# Revit family: STS-750_RV17_LOD_400
name_source: partatom
category: Электрооборудование
revit_build: Autodesk Revit 2017 (Build: 20170118_1100(x64)
units: mm (PartAtom-declared; Revit-internal decimal feet)

## family parameters
Всегда вертикально = Да
Конфигурация панели = Два столбца, слева направо
На основе рабочей плоскости = Нет
Общий = Нет
При загрузке вырезать с полостями = Нет
Размер круглого соединителя = Использовать диаметр
Тип детали = Щит
Точка расчета площади = Нет

## types (1)
- STS-750
    ADSK_URL страницы изделия = https://stilsoft.ru
    ADSK_Единица измерения = шт.
    ADSK_Завод-изготовитель = ООО «Основа Безопасности»
    ADSK_Количество = 1
    ADSK_Марка = CТАЕ.425723.001-01
    ADSK_Масса = 1.4
    ADSK_Наименование = STS-750
    ADSK_Размер_Высота = 185 мм
    ADSK_Размер_Глубина = 53 мм
    ADSK_Размер_Ширина = 93 мм
    Встроенная видеокамера = цветная
    Дальность действия ИК подсветки, м = 1
    Диапазон рабочих температур, °С = от -40 до + 50
    Интерфейс связи = 10BaseT/100BaseTX Ethernet
    Максимальное разрешение, пикс. = 1920х1080
    Мощность = 3
    Напряжение = 12
    Потребляемый ток, не более, А = 1 А
    Разрешающая способность = 2
    Режим работы = непрерывный
    Стандарт питания = Passive РоЕ, 12 В
